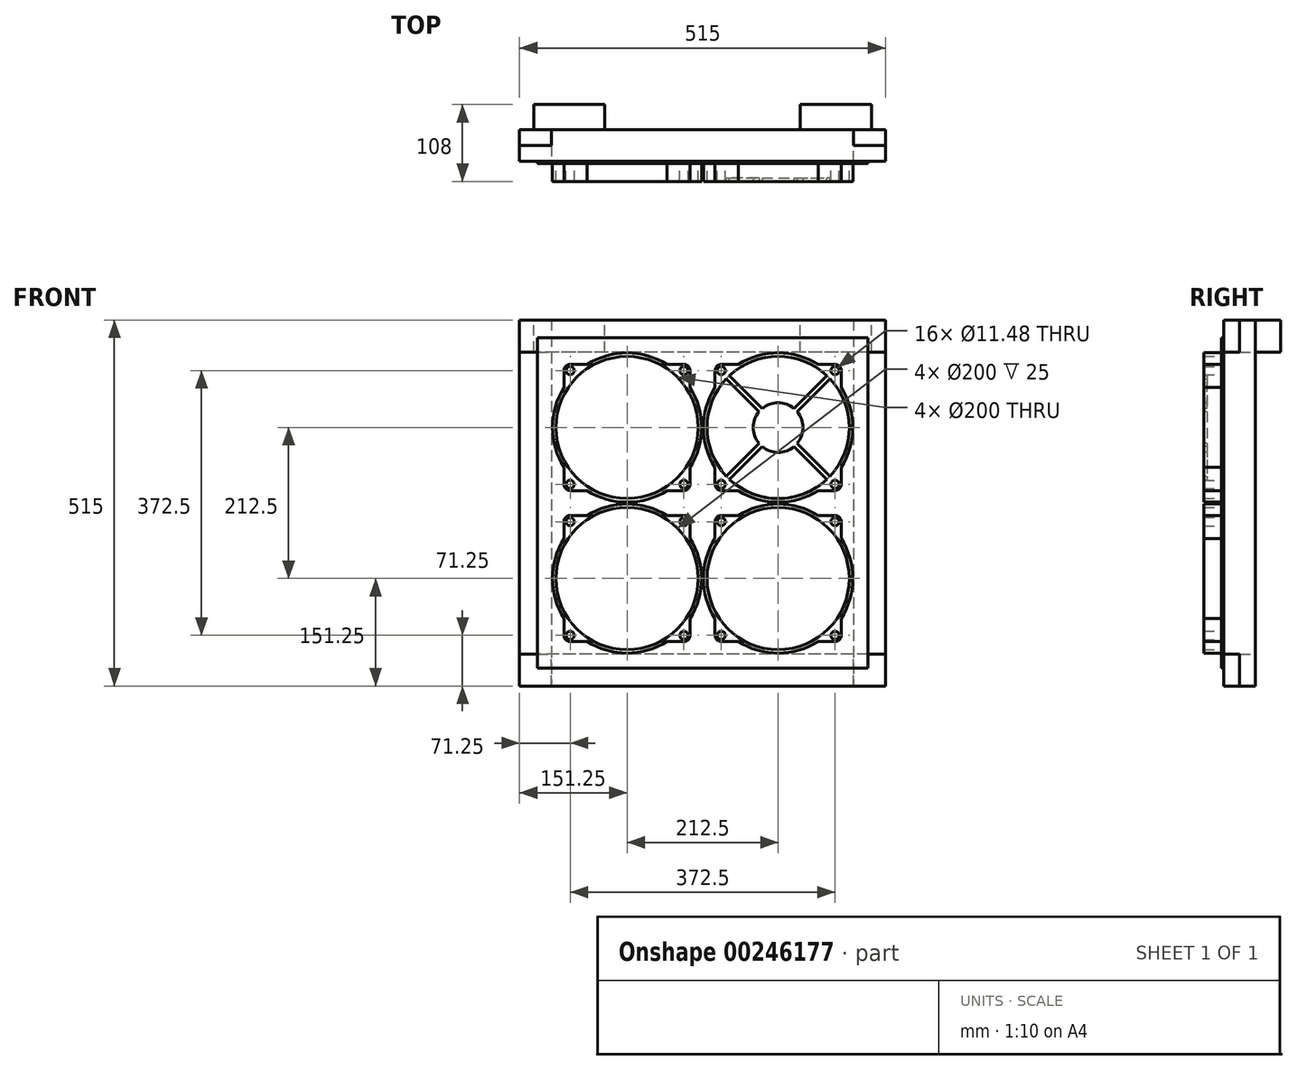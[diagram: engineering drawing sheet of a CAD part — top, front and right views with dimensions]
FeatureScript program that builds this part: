
annotation { "Feature Type Name" : "Feature", "Feature Type Description" : "" }
export const myFeature = defineFeature(function(context is Context, id is Id, definition is map)
    precondition{}
    {
        {
            assignVariable(context, id + "F0", {"name" : "HoleWidth", "anyValue" : 495});
        }
        {
            assignVariable(context, id + "F1", {"name" : "Width", "anyValue" : getVariable(context, 'HoleWidth') + 2 * 10});
        }
        {
            assignVariable(context, id + "F2", {"name" : "Height", "anyValue" : getVariable(context, 'HoleWidth') + 2 * 10});
        }
        {
            assignVariable(context, id + "F3", {"name" : "Thickness", "anyValue" : 80});
        }
        {
            var Q0;
            Q0=qCreatedBy(makeId("Top.planeOp"),FACE);
            cPlane(context, id + "F4", {"entities" : qUnion([Q0]), "cplaneType" : CPlaneType.OFFSET, "offset" : (getVariable(context, 'Height') / 2 - 45) * mm, "width" : 150 * mm, "height" : 150 * mm});
        }
        {
            var Q0;
            Q0=qCreatedBy(id+"F4.planeOp",FACE);
            var sketch = newSketch(context, id + "F5", { "sketchPlane" : qUnion([Q0])});
            skLineSegment(sketch, "E0.bottom", {"start": v(257.5, -22.5) * mm, "end": v(-257.5, -22.5) * mm});
            skLineSegment(sketch, "E0.top", {"start": v(212.5, 22.5) * mm, "end": v(-212.5, 22.5) * mm});
            skLineSegment(sketch, "E0.left", {"start": v(257.5, -22.5) * mm, "end": v(257.5, 0) * mm});
            skLineSegment(sketch, "E0.right", {"start": v(-257.5, -22.5) * mm, "end": v(-257.5, 0) * mm});
            skPoint(sketch, "E0.middle", {"position": v(0, 0) * mm});
            skLineSegment(sketch, "E1", {"start": v(-257.5, 0) * mm, "end": v(-212.5, 0) * mm});
            skPoint(sketch, "E1.endSnap0", {"position": v(-257.5, 0) * mm});
            skLineSegment(sketch, "E2", {"start": v(-212.5, 0) * mm, "end": v(-212.5, 22.5) * mm});
            skLineSegment(sketch, "E3", {"start": v(257.5, 0) * mm, "end": v(212.5, 0) * mm});
            skPoint(sketch, "E3.endSnap0", {"position": v(257.5, 0) * mm});
            skLineSegment(sketch, "E4", {"start": v(212.5, 0) * mm, "end": v(212.5, 22.5) * mm});
            skPoint(sketch, "E5.orphan", {"position": v(-257.5, 22.5) * mm});
            skPoint(sketch, "E6.orphan", {"position": v(257.5, 22.5) * mm});
            skSolve(sketch);
        }
        {
            var Q0;
            Q0 = qSketchRegion(id + "F5", true);
            extrude(context, id + "F6", {"entities" : qUnion([Q0]), "depth" : 45 * mm});
        }
        {
            var Q0;
            Q0=makeQuery(id+"F6.opExtrude","SWEPT_BODY",BODY,{"disambiguationData":[OSD([sQuery(id+"F5.wireOp",EDGE,"E0.bottom"),sQuery(id+"F5.wireOp",EDGE,"E0.top"),sQuery(id+"F5.wireOp",EDGE,"E0.left"),sQuery(id+"F5.wireOp",EDGE,"E0.right"),sQuery(id+"F5.wireOp",EDGE,"E1"),sQuery(id+"F5.wireOp",EDGE,"E2"),sQuery(id+"F5.wireOp",EDGE,"E3"),sQuery(id+"F5.wireOp",EDGE,"E4")])]});
            var Q1;
            Q1=qCreatedBy(makeId("Top.planeOp"),FACE);
            mirror(context, id + "F7", {"entities" : qUnion([Q0]), "mirrorPlane" : qUnion([Q1])});
        }
        {
            var Q0;
            Q0=qCreatedBy(makeId("Right.planeOp"),FACE);
            cPlane(context, id + "F8", {"entities" : qUnion([Q0]), "cplaneType" : CPlaneType.OFFSET, "offset" : (getVariable(context, 'Width') / 2 - 45) * mm, "width" : 150 * mm, "height" : 150 * mm});
        }
        {
            var Q0;
            Q0=qCreatedBy(id+"F8.planeOp",FACE);
            var sketch = newSketch(context, id + "F9", { "sketchPlane" : qUnion([Q0])});
            skLineSegment(sketch, "E7.bottom", {"start": v(22.5, 257.5) * mm, "end": v(-22.5, 257.5) * mm});
            skLineSegment(sketch, "E7.top", {"start": v(22.5, -257.5) * mm, "end": v(-22.5, -257.5) * mm});
            skLineSegment(sketch, "E7.left", {"start": v(22.5, 257.5) * mm, "end": v(22.5, -257.5) * mm});
            skLineSegment(sketch, "E7.right", {"start": v(-22.5, 257.5) * mm, "end": v(-22.5, -257.5) * mm});
            skSolve(sketch);
        }
        {
            var Q0;
            Q0 = qSketchRegion(id + "F9", true);
            extrude(context, id + "F10", {"entities" : qUnion([Q0]), "depth" : 45 * mm});
        }
        {
            var Q0;
            Q0=makeQuery(id+"F6.opExtrude","SWEPT_BODY",BODY,{"disambiguationData":[OSD([sQuery(id+"F5.wireOp",EDGE,"E0.bottom"),sQuery(id+"F5.wireOp",EDGE,"E0.top"),sQuery(id+"F5.wireOp",EDGE,"E0.left"),sQuery(id+"F5.wireOp",EDGE,"E0.right"),sQuery(id+"F5.wireOp",EDGE,"E1"),sQuery(id+"F5.wireOp",EDGE,"E2"),sQuery(id+"F5.wireOp",EDGE,"E3"),sQuery(id+"F5.wireOp",EDGE,"E4")])]});
            var Q1;
            Q1=makeQuery(id+"F7.opPattern","COPY",BODY,{"derivedFrom":makeQuery(id+"F6.opExtrude","SWEPT_BODY",BODY,{"disambiguationData":[OSD([sQuery(id+"F5.wireOp",EDGE,"E0.bottom"),sQuery(id+"F5.wireOp",EDGE,"E0.top"),sQuery(id+"F5.wireOp",EDGE,"E0.left"),sQuery(id+"F5.wireOp",EDGE,"E0.right"),sQuery(id+"F5.wireOp",EDGE,"E1"),sQuery(id+"F5.wireOp",EDGE,"E2"),sQuery(id+"F5.wireOp",EDGE,"E3"),sQuery(id+"F5.wireOp",EDGE,"E4")])]}),"instanceName":"1"});
            var Q2;
            Q2=makeQuery(id+"F10.opExtrude","SWEPT_BODY",BODY,{"disambiguationData":[OSD([sQuery(id+"F9.wireOp",EDGE,"E7.bottom"),sQuery(id+"F9.wireOp",EDGE,"E7.top"),sQuery(id+"F9.wireOp",EDGE,"E7.left"),sQuery(id+"F9.wireOp",EDGE,"E7.right")])]});
            booleanBodies(context, id + "F11", {"operationType" : BooleanOperationType.SUBTRACTION, "tools" : qUnion([Q0, Q1]), "targets" : qUnion([Q2]), "keepTools" : true});
        }
        {
            var Q0;
            Q0=makeQuery(id+"F10.opExtrude","SWEPT_BODY",BODY,{"disambiguationData":[OSD([sQuery(id+"F9.wireOp",EDGE,"E7.bottom"),sQuery(id+"F9.wireOp",EDGE,"E7.top"),sQuery(id+"F9.wireOp",EDGE,"E7.left"),sQuery(id+"F9.wireOp",EDGE,"E7.right")])]});
            var Q1;
            Q1=qCreatedBy(makeId("Right.planeOp"),FACE);
            mirror(context, id + "F12", {"entities" : qUnion([Q0]), "mirrorPlane" : qUnion([Q1])});
        }
        {
            var Q0;
            Q0=makeQuery(id+"F10.opExtrude","SWEPT_FACE",FACE,{"disambiguationData":[OSD([sQuery(id+"F9.wireOp",EDGE,"E7.left")])]});
            var sketch = newSketch(context, id + "F13", { "sketchPlane" : qUnion([Q0])});
            skLineSegment(sketch, "E8.bottom", {"start": v(-237.5, 212.5) * mm, "end": v(-137.5, 212.5) * mm});
            skLineSegment(sketch, "E8.top", {"start": v(-237.5, 257.5) * mm, "end": v(-137.5, 257.5) * mm});
            skLineSegment(sketch, "E8.left", {"start": v(-237.5, 212.5) * mm, "end": v(-237.5, 257.5) * mm});
            skLineSegment(sketch, "E8.right", {"start": v(-137.5, 212.5) * mm, "end": v(-137.5, 257.5) * mm});
            skLineSegment(sketch, "E9.bottom", {"start": v(137.5, 212.5) * mm, "end": v(237.5, 212.5) * mm});
            skLineSegment(sketch, "E9.top", {"start": v(137.5, 257.5) * mm, "end": v(237.5, 257.5) * mm});
            skLineSegment(sketch, "E9.left", {"start": v(137.5, 212.5) * mm, "end": v(137.5, 257.5) * mm});
            skLineSegment(sketch, "E9.right", {"start": v(237.5, 212.5) * mm, "end": v(237.5, 257.5) * mm});
            skSolve(sketch);
        }
        {
            var Q0;
            Q0 = qSketchRegion(id + "F13", true);
            extrude(context, id + "F14", {"entities" : qUnion([Q0]), "depth" : (getVariable(context, 'Thickness') - 45) * mm});
        }
        {
            var Q0;
            Q0=makeQuery(id+"F6.opExtrude","SWEPT_FACE",FACE,{"disambiguationData":[OSD([sQuery(id+"F5.wireOp",EDGE,"E0.bottom")])]});
            var sketch = newSketch(context, id + "F15", { "sketchPlane" : qUnion([Q0])});
            skLineSegment(sketch, "E10.bottom", {"start": v(-232.5, -232.5) * mm, "end": v(232.5, -232.5) * mm});
            skLineSegment(sketch, "E10.top", {"start": v(-232.5, 232.5) * mm, "end": v(232.5, 232.5) * mm});
            skLineSegment(sketch, "E10.left", {"start": v(-232.5, -232.5) * mm, "end": v(-232.5, 232.5) * mm});
            skLineSegment(sketch, "E10.right", {"start": v(232.5, -232.5) * mm, "end": v(232.5, 232.5) * mm});
            skPoint(sketch, "E10.middle", {"position": v(0, 0) * mm});
            skSolve(sketch);
        }
        {
            var Q0;
            Q0 = qSketchRegion(id + "F15", true);
            extrude(context, id + "F16", {"entities" : qUnion([Q0]), "depth" : 3 * mm});
        }
        {
            var Q0;
            Q0=makeQuery(id+"F16.opExtrude","CAP_FACE",FACE,{"disambiguationData":[OSD([sQuery(id+"F15.wireOp",EDGE,"E10.bottom"),sQuery(id+"F15.wireOp",EDGE,"E10.top"),sQuery(id+"F15.wireOp",EDGE,"E10.left"),sQuery(id+"F15.wireOp",EDGE,"E10.right")])],"isStart":false});
            var sketch = newSketch(context, id + "F17", { "sketchPlane" : qUnion([Q0])});
            skCircle(sketch, "E11", {"center": v(106.25, 106.25) * mm, "radius": 100 * mm});
            skCircle(sketch, "E12", {"center": v(106.25, -106.25) * mm, "radius": 100 * mm});
            skCircle(sketch, "E13", {"center": v(-106.25, -106.25) * mm, "radius": 100 * mm});
            skCircle(sketch, "E14", {"center": v(-106.25, 106.25) * mm, "radius": 100 * mm});
            skLineSegment(sketch, "E15", {"start": v(106.25, 106.25) * mm, "end": v(106.25, -106.25) * mm, "construction": true});
            skLineSegment(sketch, "E16", {"start": v(106.25, -106.25) * mm, "end": v(-106.25, -106.25) * mm, "construction": true});
            skLineSegment(sketch, "E17", {"start": v(-106.25, -106.25) * mm, "end": v(-106.25, 106.25) * mm, "construction": true});
            skLineSegment(sketch, "E18", {"start": v(106.25, 106.25) * mm, "end": v(-106.25, 106.25) * mm, "construction": true});
            skLineSegment(sketch, "E19", {"start": v(0, 0) * mm, "end": v(0, 361.65) * mm, "construction": true});
            skLineSegment(sketch, "E20", {"start": v(0, 0) * mm, "end": v(296.33, 0) * mm, "construction": true});
            skSolve(sketch);
        }
        {
            var Q0;
            Q0 = qSketchRegion(id + "F17", true);
            extrude(context, id + "F18", {"entities" : qUnion([Q0]), "operationType" : NewBodyOperationType.REMOVE, "endBound" : BoundingType.THROUGH_ALL, "oppositeDirection" : true, "depth" : 25 * mm});
        }
        {
            var Q0;
            Q0=makeQuery(id+"F16.opExtrude","CAP_FACE",FACE,{"disambiguationData":[OSD([sQuery(id+"F15.wireOp",EDGE,"E10.bottom"),sQuery(id+"F15.wireOp",EDGE,"E10.top"),sQuery(id+"F15.wireOp",EDGE,"E10.left"),sQuery(id+"F15.wireOp",EDGE,"E10.right")])],"isStart":false});
            var sketch = newSketch(context, id + "F19", { "sketchPlane" : qUnion([Q0])});
            skCircle(sketch, "E21.0", {"center": v(-106.25, 106.25) * mm, "radius": 100 * mm});
            skCircle(sketch, "E22", {"center": v(-106.25, 106.25) * mm, "radius": 105 * mm});
            skCircle(sketch, "E23", {"center": v(-186.25, 186.25) * mm, "radius": 5.74 * mm});
            skCircle(sketch, "E24", {"center": v(-26.25, 186.25) * mm, "radius": 5.74 * mm});
            skCircle(sketch, "E25", {"center": v(-26.25, 26.25) * mm, "radius": 5.74 * mm});
            skCircle(sketch, "E26", {"center": v(-186.25, 26.25) * mm, "radius": 5.74 * mm});
            skLineSegment(sketch, "E27", {"start": v(-186.25, 186.25) * mm, "end": v(-26.25, 186.25) * mm, "construction": true});
            skLineSegment(sketch, "E28", {"start": v(-26.25, 26.25) * mm, "end": v(-26.25, 186.25) * mm, "construction": true});
            skLineSegment(sketch, "E29", {"start": v(-26.25, 26.25) * mm, "end": v(-186.25, 26.25) * mm, "construction": true});
            skLineSegment(sketch, "E30", {"start": v(-186.25, 26.25) * mm, "end": v(-186.25, 186.25) * mm, "construction": true});
            skLineSegment(sketch, "E31", {"start": v(-106.25, 106.25) * mm, "end": v(-106.25, 243.68) * mm, "construction": true});
            skLineSegment(sketch, "E32", {"start": v(-106.25, 106.25) * mm, "end": v(-249.26, 106.25) * mm, "construction": true});
            skLineSegment(sketch, "E33", {"start": v(-194.93, 162.46) * mm, "end": v(-194.93, 186.25) * mm});
            skLineSegment(sketch, "E34", {"start": v(-162.46, 194.93) * mm, "end": v(-186.25, 194.93) * mm});
            skArc(sketch, "E35", {"start": v(-186.25, 194.93) * mm, "mid": v(-192.4, 192.4) * mm, "end": v(-194.93, 186.25) * mm});
            skArc(sketch, "E36", {"start": v(-162.46, 194.93) * mm, "mid": v(-180.5, 180.5) * mm, "end": v(-194.93, 162.46) * mm});
            skArc(sketch, "E37.MirrorCS", {"start": v(-26.25, 194.93) * mm, "mid": v(-20.1, 192.4) * mm, "end": v(-17.57, 186.25) * mm});
            skLineSegment(sketch, "E38.MirrorCS", {"start": v(-17.57, 162.46) * mm, "end": v(-17.57, 186.25) * mm});
            skArc(sketch, "E39.MirrorCS", {"start": v(-50.04, 194.93) * mm, "mid": v(-32, 180.5) * mm, "end": v(-17.57, 162.46) * mm});
            skLineSegment(sketch, "E40.MirrorCS", {"start": v(-50.04, 194.93) * mm, "end": v(-26.25, 194.93) * mm});
            skArc(sketch, "E41.MirrorCS", {"start": v(-186.25, 17.57) * mm, "mid": v(-192.4, 20.1) * mm, "end": v(-194.93, 26.25) * mm});
            skLineSegment(sketch, "E42.MirrorCS", {"start": v(-194.93, 50.04) * mm, "end": v(-194.93, 26.25) * mm});
            skArc(sketch, "E43.MirrorCS", {"start": v(-162.46, 17.57) * mm, "mid": v(-180.5, 32) * mm, "end": v(-194.93, 50.04) * mm});
            skLineSegment(sketch, "E44.MirrorCS", {"start": v(-162.46, 17.57) * mm, "end": v(-186.25, 17.57) * mm});
            skLineSegment(sketch, "E45.MirrorCS", {"start": v(-50.04, 17.57) * mm, "end": v(-26.25, 17.57) * mm});
            skLineSegment(sketch, "E46.MirrorCS", {"start": v(-17.57, 50.04) * mm, "end": v(-17.57, 26.25) * mm});
            skArc(sketch, "E47.MirrorCS", {"start": v(-26.25, 17.57) * mm, "mid": v(-20.1, 20.1) * mm, "end": v(-17.57, 26.25) * mm});
            skArc(sketch, "E48.MirrorCS", {"start": v(-50.04, 17.57) * mm, "mid": v(-32, 32) * mm, "end": v(-17.57, 50.04) * mm});
            skSolve(sketch);
        }
        {
            var Q0;
            Q0 = qSketchRegion(id + "F19", true);
            extrude(context, id + "F20", {"entities" : qUnion([Q0]), "depth" : 25 * mm});
        }
        {
            var Q0;
            Q0=makeQuery(id+"F20.opExtrude","SWEPT_BODY",BODY,{"disambiguationData":[OSD([sQuery(id+"F19.wireOp",EDGE,"E21.0"),sQuery(id+"F19.wireOp",EDGE,"E22"),sQuery(id+"F19.wireOp",EDGE,"E23"),sQuery(id+"F19.wireOp",EDGE,"E33"),sQuery(id+"F19.wireOp",EDGE,"E34"),sQuery(id+"F19.wireOp",EDGE,"E35"),sQuery(id+"F19.wireOp",EDGE,"E37.MirrorCS"),sQuery(id+"F19.wireOp",EDGE,"E24"),sQuery(id+"F19.wireOp",EDGE,"E38.MirrorCS"),sQuery(id+"F19.wireOp",EDGE,"E40.MirrorCS"),sQuery(id+"F19.wireOp",EDGE,"E26"),sQuery(id+"F19.wireOp",EDGE,"E41.MirrorCS"),sQuery(id+"F19.wireOp",EDGE,"E42.MirrorCS"),sQuery(id+"F19.wireOp",EDGE,"E44.MirrorCS"),sQuery(id+"F19.wireOp",EDGE,"E25"),sQuery(id+"F19.wireOp",EDGE,"E45.MirrorCS"),sQuery(id+"F19.wireOp",EDGE,"E46.MirrorCS"),sQuery(id+"F19.wireOp",EDGE,"E47.MirrorCS")])]});
            var Q1;
            Q1=qCreatedBy(makeId("Right.planeOp"),FACE);
            mirror(context, id + "F21", {"entities" : qUnion([Q0]), "mirrorPlane" : qUnion([Q1])});
        }
        {
            var Q0;
            Q0=makeQuery(id+"F20.opExtrude","SWEPT_BODY",BODY,{"disambiguationData":[OSD([sQuery(id+"F19.wireOp",EDGE,"E21.0"),sQuery(id+"F19.wireOp",EDGE,"E22"),sQuery(id+"F19.wireOp",EDGE,"E23"),sQuery(id+"F19.wireOp",EDGE,"E33"),sQuery(id+"F19.wireOp",EDGE,"E34"),sQuery(id+"F19.wireOp",EDGE,"E35"),sQuery(id+"F19.wireOp",EDGE,"E37.MirrorCS"),sQuery(id+"F19.wireOp",EDGE,"E24"),sQuery(id+"F19.wireOp",EDGE,"E38.MirrorCS"),sQuery(id+"F19.wireOp",EDGE,"E40.MirrorCS"),sQuery(id+"F19.wireOp",EDGE,"E26"),sQuery(id+"F19.wireOp",EDGE,"E41.MirrorCS"),sQuery(id+"F19.wireOp",EDGE,"E42.MirrorCS"),sQuery(id+"F19.wireOp",EDGE,"E44.MirrorCS"),sQuery(id+"F19.wireOp",EDGE,"E25"),sQuery(id+"F19.wireOp",EDGE,"E45.MirrorCS"),sQuery(id+"F19.wireOp",EDGE,"E46.MirrorCS"),sQuery(id+"F19.wireOp",EDGE,"E47.MirrorCS")])]});
            var Q1;
            Q1=makeQuery(id+"F21.opPattern","COPY",BODY,{"derivedFrom":makeQuery(id+"F20.opExtrude","SWEPT_BODY",BODY,{"disambiguationData":[OSD([sQuery(id+"F19.wireOp",EDGE,"E21.0"),sQuery(id+"F19.wireOp",EDGE,"E22"),sQuery(id+"F19.wireOp",EDGE,"E23"),sQuery(id+"F19.wireOp",EDGE,"E33"),sQuery(id+"F19.wireOp",EDGE,"E34"),sQuery(id+"F19.wireOp",EDGE,"E35"),sQuery(id+"F19.wireOp",EDGE,"E37.MirrorCS"),sQuery(id+"F19.wireOp",EDGE,"E24"),sQuery(id+"F19.wireOp",EDGE,"E38.MirrorCS"),sQuery(id+"F19.wireOp",EDGE,"E40.MirrorCS"),sQuery(id+"F19.wireOp",EDGE,"E26"),sQuery(id+"F19.wireOp",EDGE,"E41.MirrorCS"),sQuery(id+"F19.wireOp",EDGE,"E42.MirrorCS"),sQuery(id+"F19.wireOp",EDGE,"E44.MirrorCS"),sQuery(id+"F19.wireOp",EDGE,"E25"),sQuery(id+"F19.wireOp",EDGE,"E45.MirrorCS"),sQuery(id+"F19.wireOp",EDGE,"E46.MirrorCS"),sQuery(id+"F19.wireOp",EDGE,"E47.MirrorCS")])]}),"instanceName":"1"});
            var Q2;
            Q2=qCreatedBy(makeId("Top.planeOp"),FACE);
            mirror(context, id + "F22", {"entities" : qUnion([Q0, Q1]), "mirrorPlane" : qUnion([Q2])});
        }
        {
            var Q0;
            Q0=makeQuery(id+"F21.opPattern","COPY",FACE,{"derivedFrom":makeQuery(id+"F20.opExtrude","CAP_FACE",FACE,{"disambiguationData":[OSD([sQuery(id+"F19.wireOp",EDGE,"E21.0"),sQuery(id+"F19.wireOp",EDGE,"E22"),sQuery(id+"F19.wireOp",EDGE,"E23"),sQuery(id+"F19.wireOp",EDGE,"E33"),sQuery(id+"F19.wireOp",EDGE,"E34"),sQuery(id+"F19.wireOp",EDGE,"E35"),sQuery(id+"F19.wireOp",EDGE,"E37.MirrorCS"),sQuery(id+"F19.wireOp",EDGE,"E24"),sQuery(id+"F19.wireOp",EDGE,"E38.MirrorCS"),sQuery(id+"F19.wireOp",EDGE,"E40.MirrorCS"),sQuery(id+"F19.wireOp",EDGE,"E26"),sQuery(id+"F19.wireOp",EDGE,"E41.MirrorCS"),sQuery(id+"F19.wireOp",EDGE,"E42.MirrorCS"),sQuery(id+"F19.wireOp",EDGE,"E44.MirrorCS"),sQuery(id+"F19.wireOp",EDGE,"E25"),sQuery(id+"F19.wireOp",EDGE,"E45.MirrorCS"),sQuery(id+"F19.wireOp",EDGE,"E46.MirrorCS"),sQuery(id+"F19.wireOp",EDGE,"E47.MirrorCS")])],"isStart":false}),"instanceName":"1"});
            var sketch = newSketch(context, id + "F23", { "sketchPlane" : qUnion([Q0])});
            skCircle(sketch, "E49.0", {"center": v(106.25, 106.25) * mm, "radius": 100 * mm, "construction": true});
            skCircle(sketch, "E50", {"center": v(106.25, 106.25) * mm, "radius": 35 * mm});
            skCircle(sketch, "E51.0", {"center": v(186.25, 186.25) * mm, "radius": 5.74 * mm, "construction": true});
            skCircle(sketch, "E52.0", {"center": v(186.25, 26.25) * mm, "radius": 5.74 * mm, "construction": true});
            skCircle(sketch, "E53.0", {"center": v(26.25, 26.25) * mm, "radius": 5.74 * mm, "construction": true});
            skCircle(sketch, "E54.0", {"center": v(26.25, 186.25) * mm, "radius": 5.74 * mm, "construction": true});
            skLineSegment(sketch, "E55", {"start": v(26.25, 186.25) * mm, "end": v(186.25, 26.25) * mm, "construction": true});
            skLineSegment(sketch, "E56", {"start": v(186.25, 186.25) * mm, "end": v(26.25, 26.25) * mm, "construction": true});
            skLineSegment(sketch, "E57", {"start": v(177.33, 181.79) * mm, "end": v(123, 127.45) * mm});
            skLineSegment(sketch, "E58", {"start": v(123, 127.45) * mm, "end": v(127.45, 123) * mm});
            skLineSegment(sketch, "E59", {"start": v(127.45, 123) * mm, "end": v(181.94, 177.47) * mm});
            skLineSegment(sketch, "E60", {"start": v(181.94, 177.47) * mm, "end": v(177.33, 181.79) * mm});
            skLineSegment(sketch, "E61", {"start": v(181.48, 35.48) * mm, "end": v(127.28, 89.68) * mm});
            skLineSegment(sketch, "E62", {"start": v(127.28, 89.68) * mm, "end": v(122.82, 85.22) * mm});
            skLineSegment(sketch, "E63", {"start": v(122.82, 85.22) * mm, "end": v(175.42, 32.62) * mm});
            skLineSegment(sketch, "E64", {"start": v(175.42, 32.62) * mm, "end": v(181.48, 35.48) * mm});
            skLineSegment(sketch, "E65", {"start": v(35.9, 31.43) * mm, "end": v(89.68, 85.22) * mm});
            skLineSegment(sketch, "E66", {"start": v(89.68, 85.22) * mm, "end": v(85.22, 89.68) * mm});
            skLineSegment(sketch, "E67", {"start": v(85.22, 89.68) * mm, "end": v(30.96, 35.42) * mm});
            skLineSegment(sketch, "E68", {"start": v(30.96, 35.42) * mm, "end": v(35.9, 31.43) * mm});
            skLineSegment(sketch, "E69", {"start": v(30.96, 177.08) * mm, "end": v(82.71, 125.32) * mm});
            skLineSegment(sketch, "E70", {"start": v(82.71, 125.32) * mm, "end": v(87.18, 129.79) * mm});
            skLineSegment(sketch, "E71", {"start": v(87.18, 129.79) * mm, "end": v(35.17, 181.79) * mm});
            skLineSegment(sketch, "E72", {"start": v(35.17, 181.79) * mm, "end": v(30.96, 177.08) * mm});
            skSolve(sketch);
        }
        {
            var Q0;
            Q0 = qSketchRegion(id + "F23", true);
            extrude(context, id + "F24", {"entities" : qUnion([Q0]), "operationType" : NewBodyOperationType.ADD, "oppositeDirection" : true, "depth" : 5 * mm});
        }
    });
